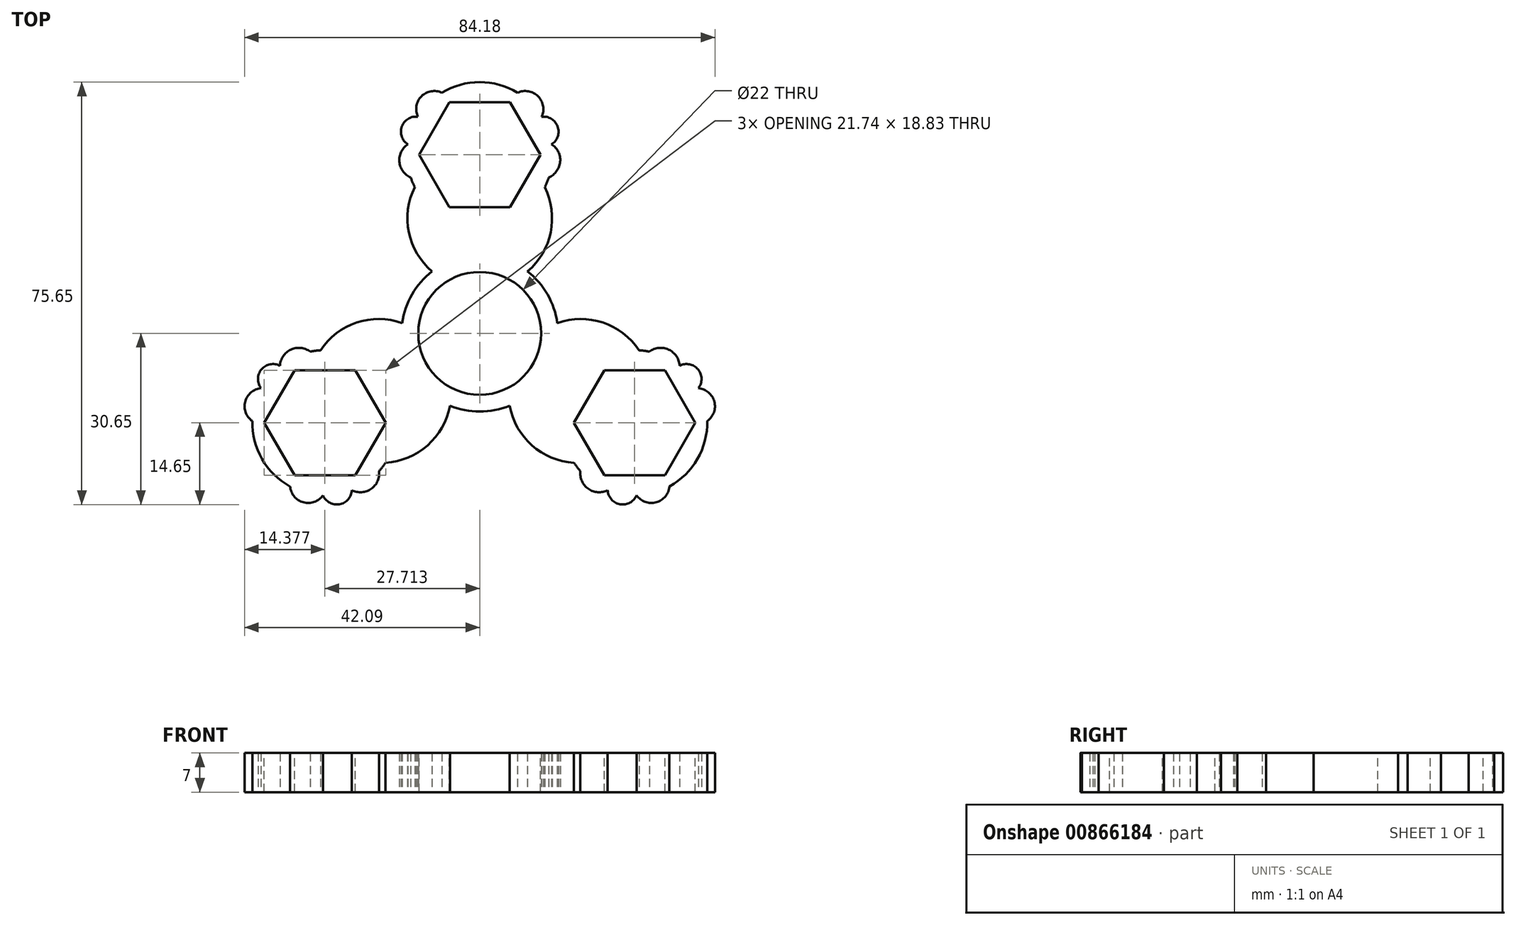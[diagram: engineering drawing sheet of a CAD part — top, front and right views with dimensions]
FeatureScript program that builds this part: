
annotation { "Feature Type Name" : "Feature", "Feature Type Description" : "" }
export const myFeature = defineFeature(function(context is Context, id is Id, definition is map)
    precondition{}
    {
        {
            var Q0;
            Q0=qCreatedBy(makeId("Top.planeOp"),FACE);
            var sketch = newSketch(context, id + "F0", { "sketchPlane" : qUnion([Q0])});
            skCircle(sketch, "E0", {"center": v(0, 0) * mm, "radius": 11 * mm});
            skCircle(sketch, "E1.0", {"center": v(0, 0) * mm, "radius": 14 * mm});
            skCircle(sketch, "E2", {"center": v(0, 0) * mm, "radius": 45 * mm, "construction": true});
            skArc(sketch, "E3", {"start": v(-12.35, 27.93) * mm, "mid": v(-12.02, 27.05) * mm, "end": v(-11.63, 26.2) * mm});
            skArc(sketch, "E4", {"start": v(-6.76, 43.1) * mm, "mid": v(-10.43, 42.46) * mm, "end": v(-11.08, 38.8) * mm});
            skArc(sketch, "E5", {"start": v(-11.08, 38.8) * mm, "mid": v(-13.95, 37.05) * mm, "end": v(-12.87, 33.87) * mm});
            skArc(sketch, "E6", {"start": v(-12.87, 33.87) * mm, "mid": v(-14.4, 30.74) * mm, "end": v(-12.35, 27.93) * mm});
            skArc(sketch, "E7", {"start": v(-11.63, 26.2) * mm, "mid": v(-12.69, 18.11) * mm, "end": v(-8.54, 11.1) * mm});
            skArc(sketch, "E8.MirrorCS", {"start": v(11.63, 26.2) * mm, "mid": v(12.69, 18.11) * mm, "end": v(8.54, 11.1) * mm});
            skArc(sketch, "E9.MirrorCS", {"start": v(12.87, 33.87) * mm, "mid": v(14.4, 30.74) * mm, "end": v(12.35, 27.93) * mm});
            skArc(sketch, "E10.MirrorCS", {"start": v(11.08, 38.8) * mm, "mid": v(13.95, 37.05) * mm, "end": v(12.87, 33.87) * mm});
            skArc(sketch, "E11.MirrorCS", {"start": v(6.76, 43.1) * mm, "mid": v(10.43, 42.46) * mm, "end": v(11.08, 38.8) * mm});
            skArc(sketch, "E12.trimOffspring", {"start": v(6.76, 43.1) * mm, "mid": v(0, 45) * mm, "end": v(-6.76, 43.1) * mm});
            skArc(sketch, "E13.trimOffspring", {"start": v(11.63, 26.2) * mm, "mid": v(12.02, 27.05) * mm, "end": v(12.35, 27.93) * mm});
            skArc(sketch, "E14.1.0", {"start": v(-40.7, -15.7) * mm, "mid": v(-38.97, -22.5) * mm, "end": v(-33.95, -27.4) * mm});
            skArc(sketch, "E14.1.1", {"start": v(-33.95, -27.4) * mm, "mid": v(-31.56, -30.26) * mm, "end": v(-28.06, -29) * mm});
            skArc(sketch, "E14.1.2", {"start": v(-28.06, -29) * mm, "mid": v(-25.11, -30.6) * mm, "end": v(-22.9, -28.08) * mm});
            skArc(sketch, "E14.1.3", {"start": v(-22.9, -28.08) * mm, "mid": v(-19.43, -27.83) * mm, "end": v(-18.01, -24.66) * mm});
            skArc(sketch, "E14.1.4", {"start": v(-16.87, -23.17) * mm, "mid": v(-9.34, -20.04) * mm, "end": v(-5.34, -12.94) * mm});
            skArc(sketch, "E14.1.5", {"start": v(-28.5, -3.02) * mm, "mid": v(-22.03, 1.93) * mm, "end": v(-13.88, 1.85) * mm});
            skArc(sketch, "E14.1.6", {"start": v(-35.76, -5.8) * mm, "mid": v(-33.82, -2.9) * mm, "end": v(-30.36, -3.27) * mm});
            skArc(sketch, "E14.1.7", {"start": v(-28.5, -3.02) * mm, "mid": v(-29.43, -3.11) * mm, "end": v(-30.36, -3.27) * mm});
            skArc(sketch, "E14.1.8", {"start": v(-18.01, -24.66) * mm, "mid": v(-17.41, -23.93) * mm, "end": v(-16.87, -23.17) * mm});
            skArc(sketch, "E14.1.9", {"start": v(-39.14, -9.8) * mm, "mid": v(-39.06, -6.45) * mm, "end": v(-35.76, -5.8) * mm});
            skArc(sketch, "E14.1.10", {"start": v(-40.7, -15.7) * mm, "mid": v(-41.99, -12.2) * mm, "end": v(-39.14, -9.8) * mm});
            skArc(sketch, "E14.2.0", {"start": v(33.95, -27.4) * mm, "mid": v(38.97, -22.5) * mm, "end": v(40.7, -15.7) * mm});
            skArc(sketch, "E14.2.1", {"start": v(40.7, -15.7) * mm, "mid": v(41.99, -12.2) * mm, "end": v(39.14, -9.8) * mm});
            skArc(sketch, "E14.2.2", {"start": v(39.14, -9.8) * mm, "mid": v(39.06, -6.45) * mm, "end": v(35.76, -5.8) * mm});
            skArc(sketch, "E14.2.3", {"start": v(35.76, -5.8) * mm, "mid": v(33.82, -2.9) * mm, "end": v(30.36, -3.27) * mm});
            skArc(sketch, "E14.2.4", {"start": v(28.5, -3.02) * mm, "mid": v(22.03, 1.93) * mm, "end": v(13.88, 1.85) * mm});
            skArc(sketch, "E14.2.5", {"start": v(16.87, -23.17) * mm, "mid": v(9.34, -20.04) * mm, "end": v(5.34, -12.94) * mm});
            skArc(sketch, "E14.2.6", {"start": v(22.9, -28.08) * mm, "mid": v(19.43, -27.83) * mm, "end": v(18.01, -24.66) * mm});
            skArc(sketch, "E14.2.7", {"start": v(16.87, -23.17) * mm, "mid": v(17.41, -23.93) * mm, "end": v(18.01, -24.66) * mm});
            skArc(sketch, "E14.2.8", {"start": v(30.36, -3.27) * mm, "mid": v(29.43, -3.11) * mm, "end": v(28.5, -3.02) * mm});
            skArc(sketch, "E14.2.9", {"start": v(28.06, -29) * mm, "mid": v(25.11, -30.6) * mm, "end": v(22.9, -28.08) * mm});
            skArc(sketch, "E14.2.10", {"start": v(33.95, -27.4) * mm, "mid": v(31.56, -30.26) * mm, "end": v(28.06, -29) * mm});
            skSolve(sketch);
        }
        {
            var Q0;
            Q0=makeQuery(id+"F0.imprint","IMPRINT",FACE,{"disambiguationData":[TD([[makeQuery(id+"F0.imprint","IMPRINT",EDGE,{"derivedFrom":sQuery(id+"F0.wireOp",EDGE,"E14.1.0")}),1.0]])]});
            var Q1;
            Q1=makeQuery(id+"F0.imprint","IMPRINT",FACE,{"disambiguationData":[TD([[makeQuery(id+"F0.imprint","IMPRINT",EDGE,{"derivedFrom":sQuery(id+"F0.wireOp",EDGE,"E0")}),-1.0]])]});
            var Q2;
            Q2=makeQuery(id+"F0.imprint","IMPRINT",FACE,{"disambiguationData":[TD([[makeQuery(id+"F0.imprint","IMPRINT",EDGE,{"derivedFrom":sQuery(id+"F0.wireOp",EDGE,"E14.2.0")}),1.0]])]});
            var Q3;
            Q3=makeQuery(id+"F0.imprint","IMPRINT",FACE,{"disambiguationData":[TD([[makeQuery(id+"F0.imprint","IMPRINT",EDGE,{"derivedFrom":sQuery(id+"F0.wireOp",EDGE,"E3")}),1.0]])]});
            extrude(context, id + "F1", {"entities" : qUnion([Q0, Q1, Q2, Q3]), "depth" : 7 * mm, "offsetDistance" : 25 * mm});
        }
        {
            var Q0;
            Q0=makeQuery(id+"F1.opExtrude","CAP_FACE",FACE,{"disambiguationData":[OSD([sQuery(id+"F0.wireOp",EDGE,"E0"),sQuery(id+"F0.wireOp",EDGE,"E1.0"),sQuery(id+"F0.wireOp",EDGE,"E3"),sQuery(id+"F0.wireOp",EDGE,"E4"),sQuery(id+"F0.wireOp",EDGE,"E5"),sQuery(id+"F0.wireOp",EDGE,"E6"),sQuery(id+"F0.wireOp",EDGE,"E7"),sQuery(id+"F0.wireOp",EDGE,"E8.MirrorCS"),sQuery(id+"F0.wireOp",EDGE,"E9.MirrorCS"),sQuery(id+"F0.wireOp",EDGE,"E10.MirrorCS"),sQuery(id+"F0.wireOp",EDGE,"E11.MirrorCS"),sQuery(id+"F0.wireOp",EDGE,"E12.trimOffspring"),sQuery(id+"F0.wireOp",EDGE,"E13.trimOffspring"),sQuery(id+"F0.wireOp",EDGE,"E14.1.0"),sQuery(id+"F0.wireOp",EDGE,"E14.1.1"),sQuery(id+"F0.wireOp",EDGE,"E14.1.2"),sQuery(id+"F0.wireOp",EDGE,"E14.1.3"),sQuery(id+"F0.wireOp",EDGE,"E14.1.4"),sQuery(id+"F0.wireOp",EDGE,"E14.1.5"),sQuery(id+"F0.wireOp",EDGE,"E14.1.6"),sQuery(id+"F0.wireOp",EDGE,"E14.1.7"),sQuery(id+"F0.wireOp",EDGE,"E14.1.8"),sQuery(id+"F0.wireOp",EDGE,"E14.1.9"),sQuery(id+"F0.wireOp",EDGE,"E14.1.10"),sQuery(id+"F0.wireOp",EDGE,"E14.2.0"),sQuery(id+"F0.wireOp",EDGE,"E14.2.1"),sQuery(id+"F0.wireOp",EDGE,"E14.2.2"),sQuery(id+"F0.wireOp",EDGE,"E14.2.3"),sQuery(id+"F0.wireOp",EDGE,"E14.2.4"),sQuery(id+"F0.wireOp",EDGE,"E14.2.5"),sQuery(id+"F0.wireOp",EDGE,"E14.2.6"),sQuery(id+"F0.wireOp",EDGE,"E14.2.7"),sQuery(id+"F0.wireOp",EDGE,"E14.2.8"),sQuery(id+"F0.wireOp",EDGE,"E14.2.9"),sQuery(id+"F0.wireOp",EDGE,"E14.2.10")])],"isStart":false});
            var sketch = newSketch(context, id + "F2", { "sketchPlane" : qUnion([Q0])});
            skCircle(sketch, "E15.cCircle", {"center": v(0, 32) * mm, "radius": 9.41 * mm, "construction": true});
            skLineSegment(sketch, "E15.0", {"start": v(-5.44, 41.41) * mm, "end": v(5.44, 41.41) * mm});
            skLineSegment(sketch, "E15.1", {"start": v(5.44, 41.41) * mm, "end": v(10.87, 32) * mm});
            skLineSegment(sketch, "E15.2", {"start": v(10.87, 32) * mm, "end": v(5.44, 22.59) * mm});
            skLineSegment(sketch, "E15.3", {"start": v(5.44, 22.59) * mm, "end": v(-5.44, 22.58) * mm});
            skLineSegment(sketch, "E15.4", {"start": v(-5.44, 22.58) * mm, "end": v(-10.87, 32) * mm});
            skLineSegment(sketch, "E15.5", {"start": v(-10.87, 32) * mm, "end": v(-5.44, 41.41) * mm});
            skPoint(sketch, "E15.0.midPoint", {"position": v(0, 41.41) * mm});
            skLineSegment(sketch, "E16.1.0", {"start": v(-33.15, -25.41) * mm, "end": v(-38.58, -16) * mm});
            skLineSegment(sketch, "E16.1.1", {"start": v(-38.58, -16) * mm, "end": v(-33.15, -6.58) * mm});
            skCircle(sketch, "E16.1.2", {"center": v(-27.71, -16) * mm, "radius": 9.41 * mm, "construction": true});
            skLineSegment(sketch, "E16.1.3", {"start": v(-33.15, -6.58) * mm, "end": v(-22.28, -6.58) * mm});
            skLineSegment(sketch, "E16.1.4", {"start": v(-22.28, -6.58) * mm, "end": v(-16.84, -16) * mm});
            skLineSegment(sketch, "E16.1.5", {"start": v(-16.84, -16) * mm, "end": v(-22.28, -25.41) * mm});
            skLineSegment(sketch, "E16.1.6", {"start": v(-22.28, -25.41) * mm, "end": v(-33.15, -25.41) * mm});
            skLineSegment(sketch, "E16.2.0", {"start": v(38.58, -16) * mm, "end": v(33.15, -25.42) * mm});
            skLineSegment(sketch, "E16.2.1", {"start": v(33.15, -25.42) * mm, "end": v(22.28, -25.42) * mm});
            skCircle(sketch, "E16.2.2", {"center": v(27.71, -16) * mm, "radius": 9.41 * mm, "construction": true});
            skLineSegment(sketch, "E16.2.3", {"start": v(22.28, -25.42) * mm, "end": v(16.84, -16) * mm});
            skLineSegment(sketch, "E16.2.4", {"start": v(16.84, -16) * mm, "end": v(22.28, -6.59) * mm});
            skLineSegment(sketch, "E16.2.5", {"start": v(22.28, -6.59) * mm, "end": v(33.15, -6.59) * mm});
            skLineSegment(sketch, "E16.2.6", {"start": v(33.15, -6.59) * mm, "end": v(38.58, -16) * mm});
            skPoint(sketch, "E16.center", {"position": v(0, 0) * mm});
            skSolve(sketch);
        }
        {
            var Q0;
            Q0=makeQuery(id+"F2.imprint","IMPRINT",FACE,{"disambiguationData":[TD([[makeQuery(id+"F2.imprint","IMPRINT",EDGE,{"derivedFrom":sQuery(id+"F2.wireOp",EDGE,"E15.0")}),-1.0]])]});
            var Q1;
            Q1=makeQuery(id+"F2.imprint","IMPRINT",FACE,{"disambiguationData":[TD([[makeQuery(id+"F2.imprint","IMPRINT",EDGE,{"derivedFrom":sQuery(id+"F2.wireOp",EDGE,"E16.1.0")}),-1.0]])]});
            var Q2;
            Q2=makeQuery(id+"F2.imprint","IMPRINT",FACE,{"disambiguationData":[TD([[makeQuery(id+"F2.imprint","IMPRINT",EDGE,{"derivedFrom":sQuery(id+"F2.wireOp",EDGE,"E16.2.0")}),-1.0]])]});
            extrude(context, id + "F3", {"entities" : qUnion([Q0, Q1, Q2]), "operationType" : NewBodyOperationType.REMOVE, "oppositeDirection" : true, "depth" : 25 * mm, "offsetDistance" : 25 * mm});
        }
    });
